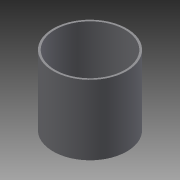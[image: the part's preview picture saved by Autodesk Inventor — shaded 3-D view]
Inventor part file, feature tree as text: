
AUTODESK INVENTOR PART (.ipt)
format: ipt  version: 2014 SP2 (Build 180246200, 246)  size: 121,856 bytes
history: native  units: in
note: dims shown in document units (in); Inventor stores cm internally (conversion verified against a paired STEP export)
features: other x84, revolve x1, sketch x1
ambient origin geometry x8: Origin, YZ Plane, XZ Plane, XY Plane, X Axis, Y Axis, Z Axis, Center Point
bodies: Solid1 (feature_tree)
feature tree (86):
  revolve  "Revolution1"  [1 undecoded]
  other  "rod_to_part_XY"
  other  "rod_to_part_YZ"
  other  "rod_to_part_ZX"
  other  "rod_to_part_X"
  other  "rod_to_part_Y"
  other  "rod_to_part_Z"
  other  "rod_to_part_Center"
  other  "to_road_XY"
  other  "to_road_YZ"
  other  "to_road_ZX"
  other  "to_road_X"
  other  "to_road_Y"
  other  "to_road_Z"
  other  "to_road_Center"
  other  "track1_XY"
  other  "track1_YZ"
  other  "track1_ZX"
  other  "track1_X"
  other  "track1_Y"
  other  "track1_Z"
  other  "track1_Center"
  other  "track1_u_XY"
  other  "track1_u_YZ"
  other  "track1_u_ZX"
  other  "track1_u_X"
  other  "track1_u_Y"
  other  "track1_u_Z"
  other  "track1_u_Center"
  other  "track2_XY"
  other  "track2_YZ"
  other  "track2_ZX"
  other  "track2_X"
  other  "track2_Y"
  other  "track2_Z"
  other  "track2_Center"
  other  "track2_u_XY"
  other  "track2_u_YZ"
  other  "track2_u_ZX"
  other  "track2_u_X"
  other  "track2_u_Y"
  other  "track2_u_Z"
  other  "track2_u_Center"
  other  "track3_XY"
  other  "track3_YZ"
  other  "track3_ZX"
  other  "track3_X"
  other  "track3_Y"
  other  "track3_Z"
  other  "track3_Center"
  other  "track3_u_XY"
  other  "track3_u_YZ"
  other  "track3_u_ZX"
  other  "track3_u_X"
  other  "track3_u_Y"
  other  "track3_u_Z"
  other  "track3_u_Center"
  other  "track4_XY"
  other  "track4_YZ"
  other  "track4_ZX"
  other  "track4_X"
  other  "track4_Y"
  other  "track4_Z"
  other  "track4_Center"
  other  "track4_u_XY"
  other  "track4_u_YZ"
  other  "track4_u_ZX"
  other  "track4_u_X"
  other  "track4_u_Y"
  other  "track4_u_Z"
  other  "track4_u_Center"
  other  "tube_rear_XY"
  other  "tube_rear_YZ"
  other  "tube_rear_ZX"
  other  "tube_rear_X"
  other  "tube_rear_Y"
  other  "tube_rear_Z"
  other  "tube_rear_Center"
  other  "tube_rod_guide_XY"
  other  "tube_rod_guide_YZ"
  other  "tube_rod_guide_ZX"
  other  "tube_rod_guide_X"
  other  "tube_rod_guide_Y"
  other  "tube_rod_guide_Z"
  other  "tube_rod_guide_Center"
  sketch  "Sketch_4"  dims[d0=360.0deg d1=0.0in d2=0.0in]
note: 1 required parameter value undecoded (feature->parameter linkage not recoverable at this tier; creation-order binding heuristic only, values carry confidence <= 0.55)
